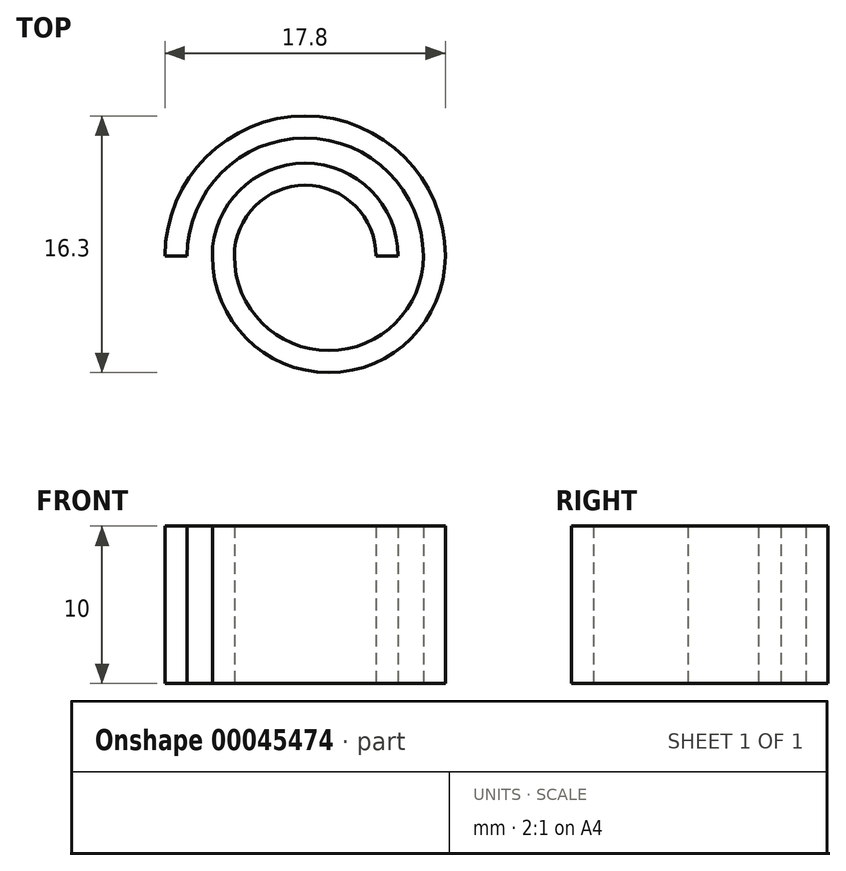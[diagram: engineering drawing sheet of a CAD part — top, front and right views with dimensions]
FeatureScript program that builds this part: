
annotation { "Feature Type Name" : "Feature", "Feature Type Description" : "" }
export const myFeature = defineFeature(function(context is Context, id is Id, definition is map)
    precondition{}
    {
        {
            var Q0;
            Q0=qCreatedBy(makeId("Top.planeOp"),FACE);
            var sketch = newSketch(context, id + "F0", { "sketchPlane" : qUnion([Q0])});
            skLineSegment(sketch, "E0", {"start": v(0, 0) * mm, "end": v(3, 0) * mm, "construction": true});
            skLineSegment(sketch, "E1", {"start": v(0, 0) * mm, "end": v(-1.5, 0) * mm, "construction": true});
            skArc(sketch, "E2", {"start": v(3, 0) * mm, "mid": v(2.17, 2.6) * mm, "end": v(0, 4.24) * mm});
            skArc(sketch, "E3", {"start": v(0, 4.24) * mm, "mid": v(-4.1, 3.67) * mm, "end": v(-6, 0) * mm});
            skArc(sketch, "E4", {"start": v(-6, 0) * mm, "mid": v(0, -6) * mm, "end": v(6, 0) * mm});
            skArc(sketch, "E5", {"start": v(6, 0) * mm, "mid": v(-1.5, 7.5) * mm, "end": v(-9, 0) * mm});
            skArc(sketch, "E6.0", {"start": v(7.4, 0) * mm, "mid": v(-1.5, 8.9) * mm, "end": v(-10.4, 0) * mm});
            skArc(sketch, "E6.1", {"start": v(-7.4, 0) * mm, "mid": v(0, -7.4) * mm, "end": v(7.4, 0) * mm});
            skArc(sketch, "E6.2", {"start": v(0.47, 5.56) * mm, "mid": v(-4.9, 4.82) * mm, "end": v(-7.4, 0) * mm});
            skArc(sketch, "E6.3", {"start": v(4.4, 0) * mm, "mid": v(3.32, 3.4) * mm, "end": v(0.47, 5.56) * mm});
            skLineSegment(sketch, "E7", {"start": v(-10.4, 0) * mm, "end": v(-9, 0) * mm});
            skLineSegment(sketch, "E8", {"start": v(3, 0) * mm, "end": v(4.4, 0) * mm});
            skSolve(sketch);
        }
        {
            var Q0;
            Q0=makeQuery(id+"F0.imprint","IMPRINT",FACE,{"disambiguationData":[TD([[makeQuery(id+"F0.imprint","IMPRINT",EDGE,{"derivedFrom":sQuery(id+"F0.wireOp",EDGE,"E2")}),-1.0]])]});
            extrude(context, id + "F1", {"entities" : qUnion([Q0]), "depth" : 10 * mm});
        }
    });
